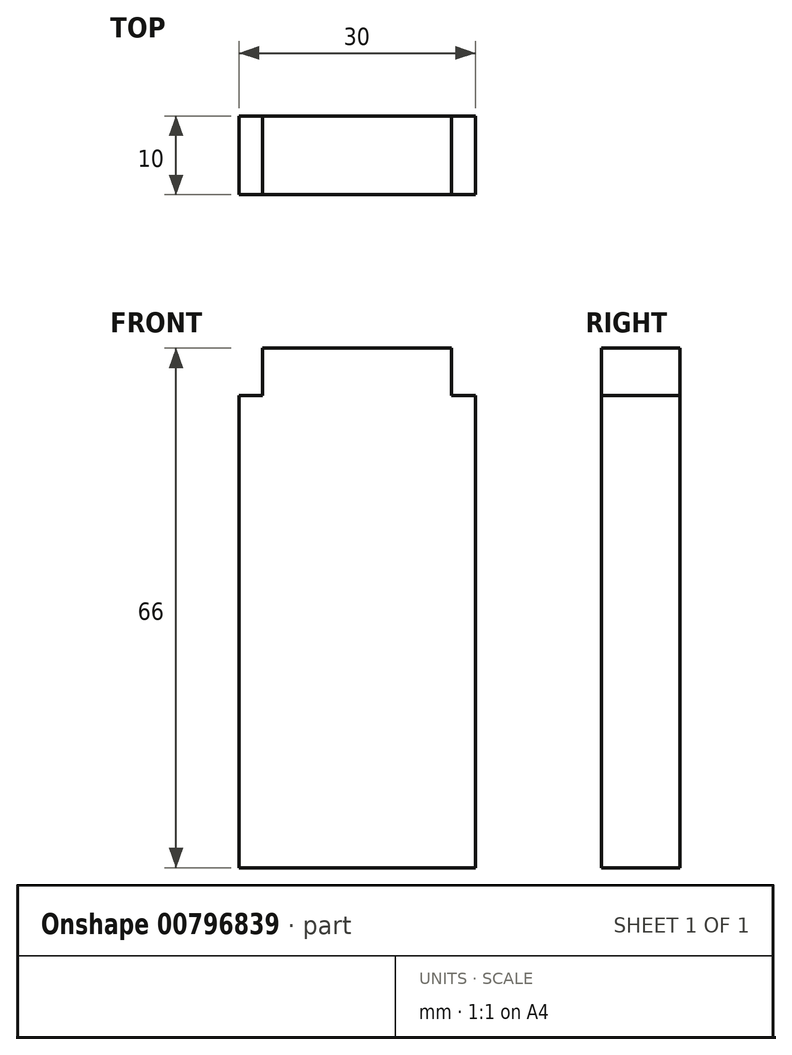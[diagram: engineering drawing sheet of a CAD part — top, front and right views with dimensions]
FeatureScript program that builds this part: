
annotation { "Feature Type Name" : "Feature", "Feature Type Description" : "" }
export const myFeature = defineFeature(function(context is Context, id is Id, definition is map)
    precondition{}
    {
        {
            var Q0;
            Q0=qCreatedBy(makeId("Top.planeOp"),FACE);
            var sketch = newSketch(context, id + "F0", { "sketchPlane" : qUnion([Q0])});
            skLineSegment(sketch, "E0.bottom", {"start": v(15, -5) * mm, "end": v(-15, -5) * mm});
            skLineSegment(sketch, "E0.top", {"start": v(15, 5) * mm, "end": v(-15, 5) * mm});
            skLineSegment(sketch, "E0.left", {"start": v(15, -5) * mm, "end": v(15, 5) * mm});
            skLineSegment(sketch, "E0.right", {"start": v(-15, -5) * mm, "end": v(-15, 5) * mm});
            skPoint(sketch, "E0.middle", {"position": v(0, 0) * mm});
            skSolve(sketch);
        }
        {
            var Q0;
            Q0 = qSketchRegion(id + "F0", true);
            extrude(context, id + "F1", {"entities" : qUnion([Q0]), "depth" : 40 * mm, "offsetDistance" : 25 * mm});
        }
        {
            var Q0;
            Q0=makeQuery(id+"F1.opExtrude","CAP_FACE",FACE,{"disambiguationData":[OSD([sQuery(id+"F0.wireOp",EDGE,"E0.bottom"),sQuery(id+"F0.wireOp",EDGE,"E0.top"),sQuery(id+"F0.wireOp",EDGE,"E0.left"),sQuery(id+"F0.wireOp",EDGE,"E0.right")])],"isStart":false});
            var sketch = newSketch(context, id + "F2", { "sketchPlane" : qUnion([Q0])});
            skLineSegment(sketch, "E1.bottom", {"start": v(15, -5) * mm, "end": v(-15, -5) * mm});
            skLineSegment(sketch, "E1.top", {"start": v(15, 5) * mm, "end": v(-15, 5) * mm});
            skLineSegment(sketch, "E1.left", {"start": v(15, -5) * mm, "end": v(15, 5) * mm});
            skLineSegment(sketch, "E1.right", {"start": v(-15, -5) * mm, "end": v(-15, 5) * mm});
            skPoint(sketch, "E1.middle", {"position": v(0, 0) * mm});
            skSolve(sketch);
        }
        {
            var Q0;
            Q0 = qSketchRegion(id + "F2", true);
            extrude(context, id + "F3", {"entities" : qUnion([Q0]), "operationType" : NewBodyOperationType.ADD, "depth" : 20 * mm, "offsetDistance" : 25 * mm});
        }
        {
            var Q0;
            Q0=makeQuery(id+"F3.opExtrude","CAP_FACE",FACE,{"disambiguationData":[OSD([sQuery(id+"F2.wireOp",EDGE,"E1.bottom"),sQuery(id+"F2.wireOp",EDGE,"E1.top"),sQuery(id+"F2.wireOp",EDGE,"E1.left"),sQuery(id+"F2.wireOp",EDGE,"E1.right")])],"isStart":false});
            var sketch = newSketch(context, id + "F4", { "sketchPlane" : qUnion([Q0])});
            skLineSegment(sketch, "E2.bottom", {"start": v(12, -5) * mm, "end": v(-12, -5) * mm});
            skLineSegment(sketch, "E2.top", {"start": v(12, 5) * mm, "end": v(-12, 5) * mm});
            skLineSegment(sketch, "E2.left", {"start": v(12, -5) * mm, "end": v(12, 5) * mm});
            skLineSegment(sketch, "E2.right", {"start": v(-12, -5) * mm, "end": v(-12, 5) * mm});
            skPoint(sketch, "E2.middle", {"position": v(0, 0) * mm});
            skSolve(sketch);
        }
        {
            var Q0;
            Q0 = qSketchRegion(id + "F4", true);
            extrude(context, id + "F5", {"entities" : qUnion([Q0]), "operationType" : NewBodyOperationType.ADD, "depth" : 6 * mm, "offsetDistance" : 25 * mm});
        }
    });
